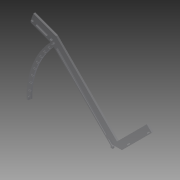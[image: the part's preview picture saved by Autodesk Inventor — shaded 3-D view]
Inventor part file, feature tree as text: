
AUTODESK INVENTOR PART (.ipt)
format: ipt  version: 2013 (Build 170138000, 138)  size: 276,480 bytes
history: native  units: in
note: dims shown in document units (in); Inventor stores cm internally (conversion verified against a paired STEP export)
features: reference x12, extrude x9, sketch x9
ambient origin geometry x8: Origin, YZ Plane, XZ Plane, XY Plane, X Axis, Y Axis, Z Axis, Center Point
bodies: Solid1 (feature_tree)
feature tree (30):
  extrude  "Extrusion1"  Depth=0.25in TaperAngle=0.0deg
  extrude  "Extrusion2"  Depth=0.25in
  extrude  "Extrusion3"  Depth=0.25in TaperAngle=0.0deg
  extrude  "Extrusion4"  Depth=1.0in
  extrude  "Extrusion7"  Depth=0.25in TaperAngle=0.0deg
  extrude  "Extrusion8"  Depth=1.375in
  extrude  "Extrusion11"  Depth=6.0in
  extrude  "Extrusion12"  Depth=0.125in
  extrude  "Extrusion13"  Depth=0.25in
  sketch  "Sketch1"  dims[d0=23.375in d1=0.25in d2=0.0in]
  sketch  "Sketch2"  dims[d3=0.25in d4=0.25in]
  sketch  "Sketch3"  dims[d5=0.25in d6=0.0in d10=0.25in d11=0.0in]
  reference  "Reference1"
  sketch  "Sketch4"  dims[d12=0.25in d13=0.0in d19=1.0in]
  reference  "Reference2"
  sketch  "Sketch7"  dims[d20=0.7043in d21=0.25in d22=0.0in]
  reference  "Reference5"
  reference  "Reference6"
  reference  "Reference7"
  reference  "Reference8"
  sketch  "Sketch8"  dims[d23=0.25in d24=0.0in d35=1.375in]
  reference  "Reference9"
  reference  "Reference10"
  reference  "Reference11"
  reference  "Reference12"
  reference  "Reference13"
  sketch  "Sketch11"  dims[d36=0.25in d37=0.0in d38=6.0in]
  sketch  "Sketch12"  dims[d39=1.0in d40=0.125in]
  sketch  "Sketch13"  dims[d41=0.5in d42=0.25in d43=0.125in d44=0.125in d45=0.5in d46=0.125in d47=0.125in d48=3.5in d49=0.25in d50=0.0in d51=1.0in d52=0.0in]
  reference  "Reference14"
